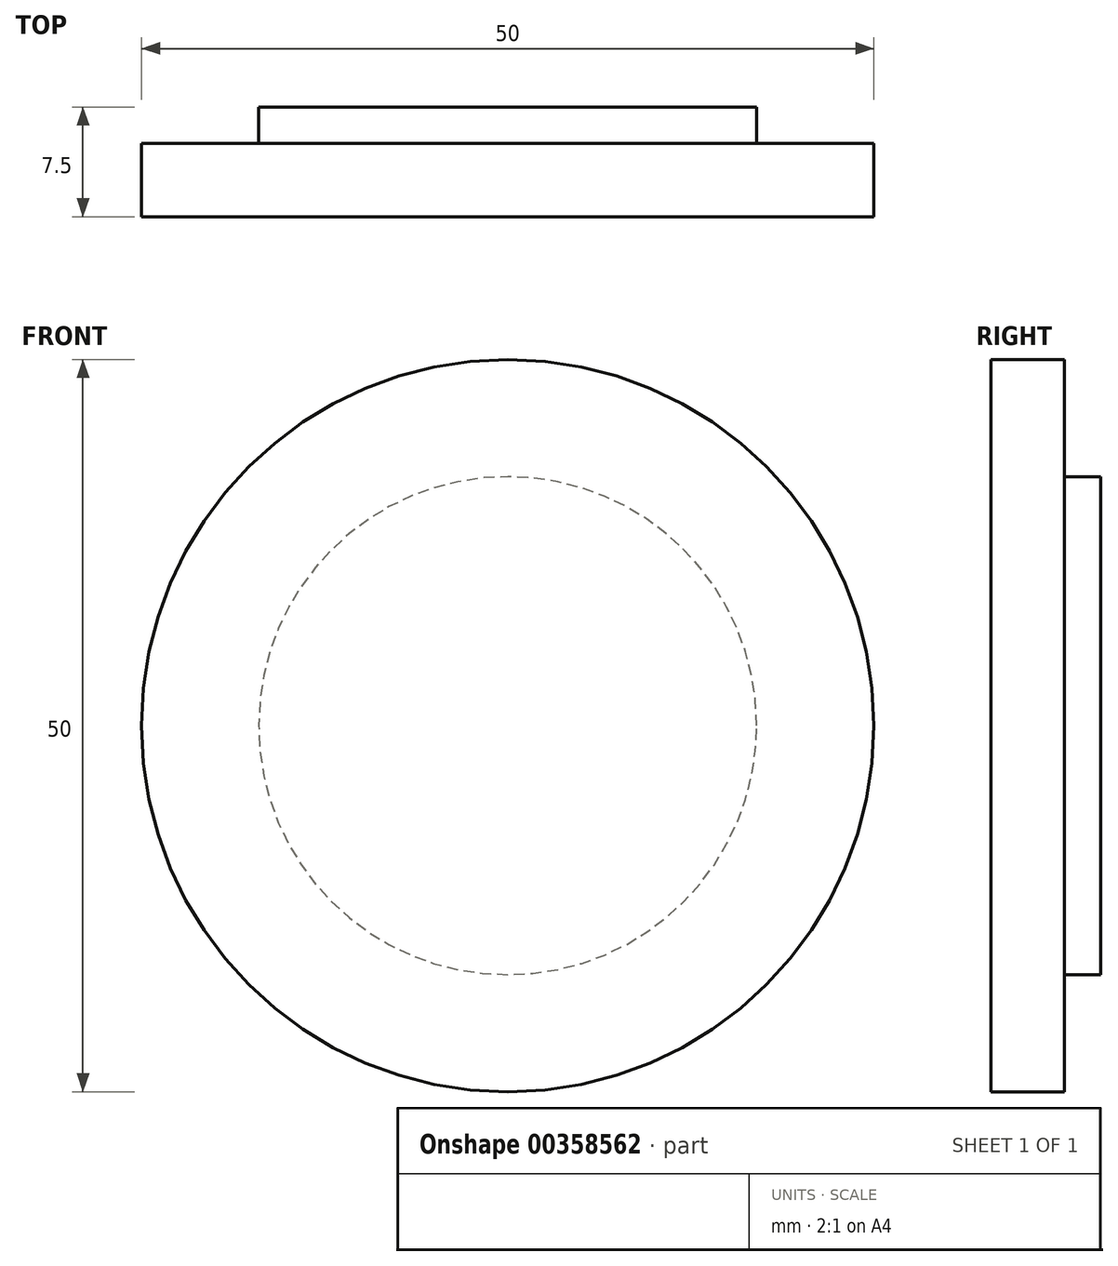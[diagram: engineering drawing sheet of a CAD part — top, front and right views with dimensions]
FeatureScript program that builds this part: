
annotation { "Feature Type Name" : "Feature", "Feature Type Description" : "" }
export const myFeature = defineFeature(function(context is Context, id is Id, definition is map)
    precondition{}
    {
        {
            var Q0;
            Q0=qCreatedBy(makeId("Front.planeOp"),FACE);
            var sketch = newSketch(context, id + "F0", { "sketchPlane" : qUnion([Q0])});
            skCircle(sketch, "E0", {"center": v(0, 0) * mm, "radius": 25 * mm});
            skSolve(sketch);
        }
        {
            var Q0;
            Q0 = qSketchRegion(id + "F0", true);
            extrude(context, id + "F1", {"entities" : qUnion([Q0]), "oppositeDirection" : true, "depth" : 7.5 * mm});
        }
        {
            var Q0;
            Q0=makeQuery(id+"F1.opExtrude","CAP_FACE",FACE,{"disambiguationData":[OSD([sQuery(id+"F0.wireOp",EDGE,"E0")])],"isStart":false});
            var sketch = newSketch(context, id + "F2", { "sketchPlane" : qUnion([Q0])});
            skCircle(sketch, "E1", {"center": v(0, 0) * mm, "radius": 17 * mm});
            skCircle(sketch, "E2", {"center": v(0, 0) * mm, "radius": 37.74 * mm});
            skSolve(sketch);
        }
        {
            var Q0;
            Q0 = qSketchRegion(id + "F2", true);
            extrude(context, id + "F3", {"entities" : qUnion([Q0]), "operationType" : NewBodyOperationType.REMOVE, "oppositeDirection" : true, "depth" : 2.5 * mm});
        }
    });
